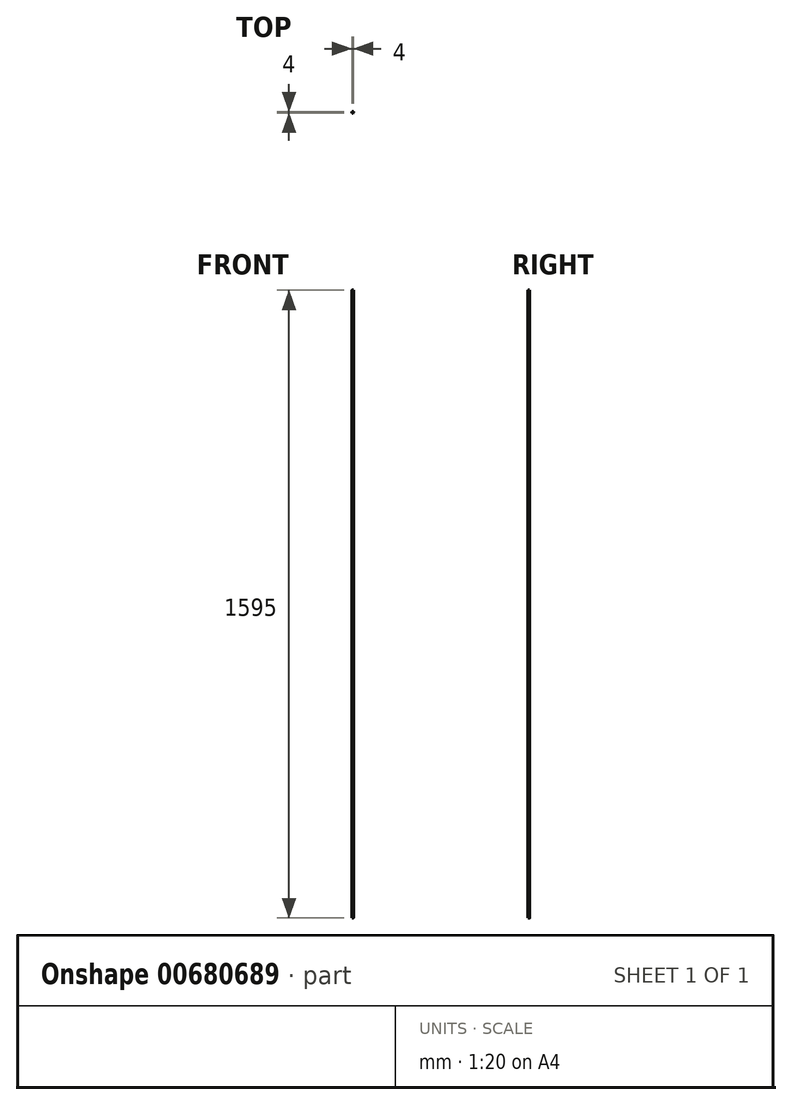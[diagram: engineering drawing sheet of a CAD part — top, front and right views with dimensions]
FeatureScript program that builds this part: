
annotation { "Feature Type Name" : "Feature", "Feature Type Description" : "" }
export const myFeature = defineFeature(function(context is Context, id is Id, definition is map)
    precondition{}
    {
        {
            var Q0;
            Q0=qCreatedBy(makeId("Top.planeOp"),FACE);
            var sketch = newSketch(context, id + "F0", { "sketchPlane" : qUnion([Q0])});
            skCircle(sketch, "E0", {"center": v(0, 0) * mm, "radius": 2 * mm});
            skSolve(sketch);
        }
        {
            var Q0;
            Q0=makeQuery(id+"F0.imprint","IMPRINT",FACE,{"disambiguationData":[TD([[makeQuery(id+"F0.imprint","IMPRINT",EDGE,{"derivedFrom":sQuery(id+"F0.wireOp",EDGE,"E0")}),1.0]])]});
            extrude(context, id + "F1", {"entities" : qUnion([Q0]), "depth" : (1520 + 75) * mm, "offsetDistance" : 25 * mm});
        }
    });
